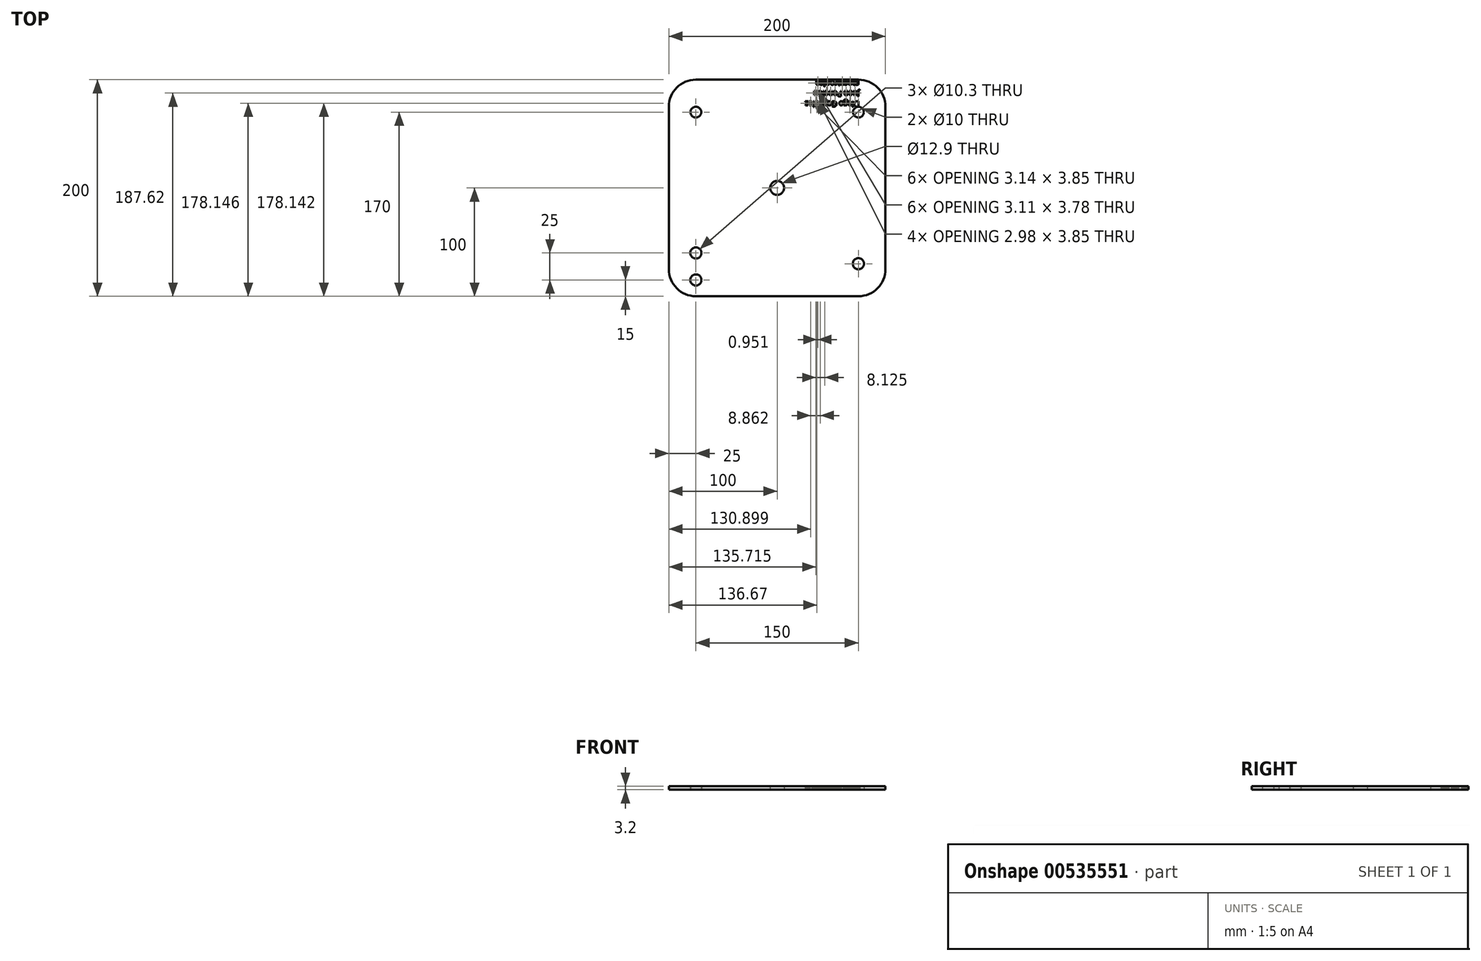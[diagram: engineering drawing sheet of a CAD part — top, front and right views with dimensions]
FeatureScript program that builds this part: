
annotation { "Feature Type Name" : "Feature", "Feature Type Description" : "" }
export const myFeature = defineFeature(function(context is Context, id is Id, definition is map)
    precondition{}
    {
        {
            var Q0;
            Q0=qCreatedBy(makeId("Top.planeOp"),FACE);
            var sketch = newSketch(context, id + "F0", { "sketchPlane" : qUnion([Q0])});
            skLineSegment(sketch, "E0.bottom", {"start": v(-75, 100) * mm, "end": v(75, 100) * mm});
            skLineSegment(sketch, "E0.top", {"start": v(-75, -100) * mm, "end": v(75, -100) * mm});
            skLineSegment(sketch, "E0.left", {"start": v(-100, 75) * mm, "end": v(-100, -75) * mm});
            skLineSegment(sketch, "E0.right", {"start": v(100, 75) * mm, "end": v(100, -75) * mm});
            skPoint(sketch, "E0.middle", {"position": v(0, 0) * mm});
            skPoint(sketch, "E1.visualSharp", {"position": v(-100, 100) * mm});
            skArc(sketch, "E1.filletArc", {"start": v(-75, 100) * mm, "mid": v(-92.68, 92.68) * mm, "end": v(-100, 75) * mm});
            skPoint(sketch, "E2.visualSharp", {"position": v(-100, -100) * mm});
            skArc(sketch, "E2.filletArc", {"start": v(-100, -75) * mm, "mid": v(-92.68, -92.68) * mm, "end": v(-75, -100) * mm});
            skPoint(sketch, "E3.visualSharp", {"position": v(100, -100) * mm});
            skArc(sketch, "E3.filletArc", {"start": v(75, -100) * mm, "mid": v(92.68, -92.68) * mm, "end": v(100, -75) * mm});
            skPoint(sketch, "E4.visualSharp", {"position": v(100, 100) * mm});
            skArc(sketch, "E4.filletArc", {"start": v(100, 75) * mm, "mid": v(92.68, 92.68) * mm, "end": v(75, 100) * mm});
            skCircle(sketch, "E5", {"center": v(0, 0) * mm, "radius": 6.45 * mm});
            skCircle(sketch, "E6", {"center": v(-75, -85) * mm, "radius": 5.15 * mm});
            skText(sketch, "E7", { "text": "Diego Gonzalez \nJuan Peneleu\nmecatronica", "fontName": "OpenSans-Regular.ttf"});
            skCircle(sketch, "E8", {"center": v(-75, -60) * mm, "radius": 5.15 * mm});
            skCircle(sketch, "E9", {"center": v(-75, 70) * mm, "radius": 5 * mm});
            skCircle(sketch, "E10.MirrorC", {"center": v(75, 70) * mm, "radius": 5 * mm});
            skCircle(sketch, "E11", {"center": v(75, -70) * mm, "radius": 5.15 * mm});
            const initialGuessF0  = {"E7": [0.07576, 0.08, -1, 0, 0.005]};
            skSetInitialGuess(sketch, initialGuessF0);
            skSolve(sketch);
        }
        {
            var Q0;
            Q0 = qSketchRegion(id + "F0", true);
            extrude(context, id + "F1", {"entities" : qUnion([Q0]), "depth" : 3.2 * mm, "offsetDistance" : 25 * mm});
        }
    });
